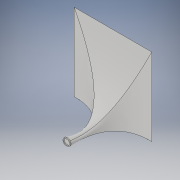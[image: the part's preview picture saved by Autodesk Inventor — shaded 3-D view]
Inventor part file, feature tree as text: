
AUTODESK INVENTOR PART (.ipt)
format: ipt  version: 2017 (Build 210142000, 142)  size: 283,136 bytes
history: native  units: in
note: dims shown in document units (in); Inventor stores cm internally (conversion verified against a paired STEP export)
features: sketch x3, extrude x2, other x2, loft x2
ambient origin geometry x8: Origin, YZ Plane, XZ Plane, XY Plane, X Axis, Y Axis, Z Axis, Center Point
bodies: Solid1 (feature_tree)
feature tree (9):
  extrude  "connection"  Depth=30.0in
  other  "front half of room"
  other  "front of room"
  sketch  "Sketch3"  dims[d17=30.0in d26=69.0in d27=59.0in d28=102.0in]
  loft  "shell make "
  loft  "shell cut"
  extrude  "connection to door"  Depth=1.0in
  sketch  "Sketch1"  dims[d12=1.0in d13=0.0in d14=30.0in]
  sketch  "Sketch5"  dims[d29=102.0in d33=1.0in d34=1.0in d35=1.0in d36=1.0in d55=100.0in d56=100.0in d57=1.0in d58=0.0in d82=4.0in d83=1.0in d84=4.8944in d85=0.5833in d86=3.8873in d87=3.8873in d88=1.7083in d89=0.0625in d90=0.0625in d91=1.6458in d92=0.125in d93=0.125in d153=6.21in d154=5.31in d157=0.0in d158=90.0deg d159=0.0in d160=90.0deg d161=0.0in d162=90.0deg d179=1.0in d180=0.0in d181=90.0deg d182=0.0in d183=90.0deg d184=0.0in d185=90.0deg d217=3.082in d218=1.0in]
